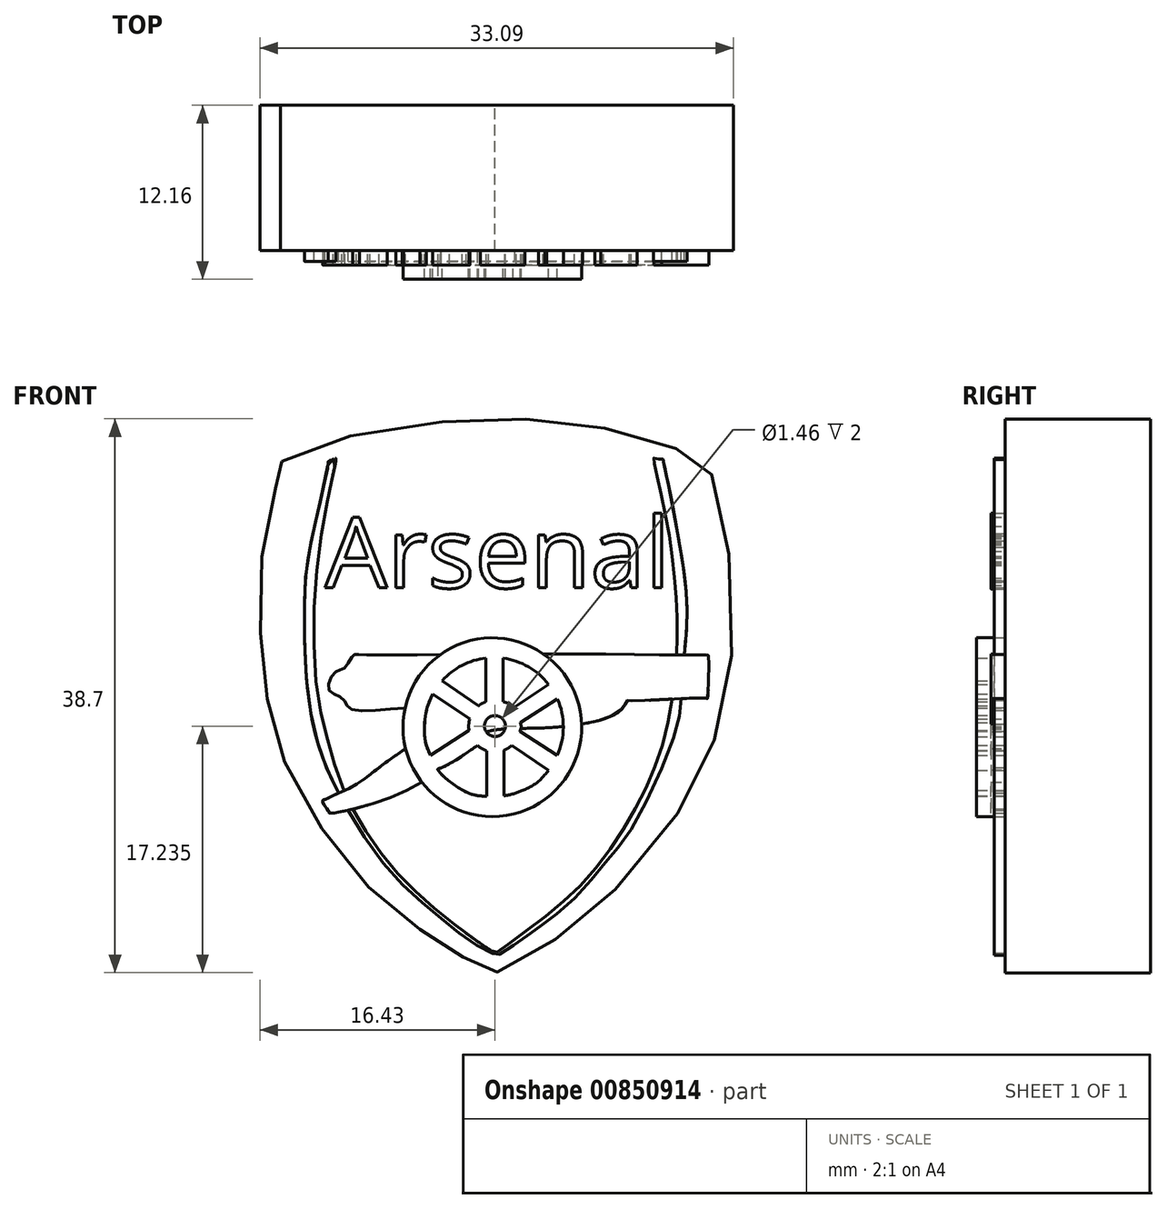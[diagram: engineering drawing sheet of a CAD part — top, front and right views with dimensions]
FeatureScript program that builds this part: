
annotation { "Feature Type Name" : "Feature", "Feature Type Description" : "" }
export const myFeature = defineFeature(function(context is Context, id is Id, definition is map)
    precondition{}
    {
        {
            var Q0;
            Q0=qCreatedBy(makeId("Front.planeOp"),FACE);
            var sketch = newSketch(context, id + "F0", { "sketchPlane" : qUnion([Q0])});
            skPoint(sketch, "E0.12.internal.snap0", {"position": v(20, 0) * mm});
            skPoint(sketch, "E0.13.internal.snap0", {"position": v(20, 0) * mm});
            skFitSpline(sketch, "E0", {"points": [v(5.13, 36.38) * mm, v(10.44, 38.27) * mm, v(18.73, 39.3) * mm, v(25.28, 39.07) * mm, v(31.25, 37.76) * mm, v(34.45, 36.38) * mm, v(35.25, 35.22) * mm, v(36.63, 27) * mm, v(35.76, 18.33) * mm, v(33.07, 12.22) * mm, v(27.1, 5.16) * mm, v(22.66, 2.04) * mm, v(20, 0.64) * mm, v(20, 0.66) * mm, v(18.14, 1.55) * mm, v(16.5, 2.5) * mm, v(13.05, 4.95) * mm, v(9.94, 7.99) * mm, v(6.24, 13.42) * mm, v(4.58, 17.65) * mm, v(3.79, 21.95) * mm, v(3.6, 26.79) * mm, v(4.19, 32.94) * mm, v(4.98, 35.32) * mm, v(5.05, 35.81) * mm, v(5.13, 36.38) * mm]});
            skSolve(sketch);
        }
        {
            var Q0;
            Q0=makeQuery(id+"F0.imprint","IMPRINT",FACE,{"disambiguationData":[TD([[makeQuery(id+"F0.imprint","IMPRINT",EDGE,{"derivedFrom":sQuery(id+"F0.wireOp",EDGE,"E0")}),-1.0]])]});
            extrude(context, id + "F1", {"entities" : qUnion([Q0]), "depth" : 10.16 * mm, "offsetDistance" : 25 * mm});
        }
        {
            var Q0;
            {var subQ0=sQuery(id+"F0.wireOp",EDGE,"E0");Q0=makeQuery(id+"FBtWP9GjsR8Dhei_1.boolean.opBoolean","SPLIT",FACE,{"disambiguationData":[TD([makeQuery(id+"F1.opExtrude","SWEPT_FACE",FACE,{"disambiguationData":[OSD([subQ0])]})])],"derivedFrom":makeQuery(id+"F1.opExtrude","CAP_FACE",FACE,{"disambiguationData":[OSD([subQ0])],"isStart":false})});}
            var sketch = newSketch(context, id + "F2", { "sketchPlane" : qUnion([Q0])});
            skCircle(sketch, "E1", {"center": v(19.82, 17.8) * mm, "radius": 6.24 * mm});
            skPoint(sketch, "E1.first.point", {"position": v(19.26, 24.01) * mm});
            skPoint(sketch, "E1.second.point", {"position": v(20.58, 11.6) * mm});
            skPoint(sketch, "E1.third.point", {"position": v(24.98, 14.28) * mm});
            skArc(sketch, "E2", {"start": v(19.38, 22.63) * mm, "mid": v(17.7, 22.12) * mm, "end": v(16.32, 21.05) * mm});
            skPoint(sketch, "E2.first.point", {"position": v(21.94, 13.38) * mm});
            skPoint(sketch, "E2.second.point", {"position": v(17.75, 22.14) * mm});
            skPoint(sketch, "E2.third.point", {"position": v(23, 21.57) * mm});
            skPoint(sketch, "E3.first.point", {"position": v(20.88, 19.43) * mm});
            skPoint(sketch, "E3.second.point", {"position": v(18.17, 17.84) * mm});
            skPoint(sketch, "E3.third.point", {"position": v(18.99, 16.36) * mm});
            skCircle(sketch, "E4", {"center": v(20, 17.87) * mm, "radius": 0.73 * mm});
            skPoint(sketch, "E4.first.point", {"position": v(20.04, 17.14) * mm});
            skPoint(sketch, "E4.second.point", {"position": v(19.68, 18.53) * mm});
            skPoint(sketch, "E4.third.point", {"position": v(20.7, 18.1) * mm});
            skLineSegment(sketch, "E5", {"start": v(16.32, 21.05) * mm, "end": v(18.86, 19.29) * mm});
            skLineSegment(sketch, "E6", {"start": v(15.67, 20.13) * mm, "end": v(18.24, 18.37) * mm});
            skLineSegment(sketch, "E7", {"start": v(15.48, 15.84) * mm, "end": v(18.2, 17.58) * mm});
            skLineSegment(sketch, "E8", {"start": v(19.44, 12.97) * mm, "end": v(19.44, 16.14) * mm});
            skLineSegment(sketch, "E9", {"start": v(20.63, 16.18) * mm, "end": v(20.63, 13) * mm});
            skLineSegment(sketch, "E10", {"start": v(21.19, 16.53) * mm, "end": v(23.74, 14.78) * mm});
            skLineSegment(sketch, "E11", {"start": v(21.75, 17.52) * mm, "end": v(24.37, 15.82) * mm});
            skLineSegment(sketch, "E12", {"start": v(21.77, 18.1) * mm, "end": v(24.37, 19.78) * mm});
            skLineSegment(sketch, "E13", {"start": v(21.28, 19.13) * mm, "end": v(23.76, 20.8) * mm});
            skLineSegment(sketch, "E14", {"start": v(20.58, 19.57) * mm, "end": v(20.58, 22.62) * mm});
            skLineSegment(sketch, "E15", {"start": v(19.38, 19.57) * mm, "end": v(19.38, 22.63) * mm});
            skArc(sketch, "E16.trimOffspring", {"start": v(24.37, 15.82) * mm, "mid": v(24.79, 17.8) * mm, "end": v(24.37, 19.78) * mm});
            skArc(sketch, "E17.trimOffspring", {"start": v(20.63, 13) * mm, "mid": v(21.3, 13.14) * mm, "end": v(21.94, 13.38) * mm});
            skArc(sketch, "E18.trimOffspring", {"start": v(23.76, 20.8) * mm, "mid": v(22.35, 22.02) * mm, "end": v(20.58, 22.62) * mm});
            skArc(sketch, "E19.trimOffspring", {"start": v(20.63, 16.18) * mm, "mid": v(20.92, 16.33) * mm, "end": v(21.19, 16.53) * mm});
            skArc(sketch, "E20.trimOffspring", {"start": v(18.24, 18.37) * mm, "mid": v(18.18, 17.98) * mm, "end": v(18.2, 17.58) * mm});
            skArc(sketch, "E21.trimOffspring", {"start": v(18.79, 16.51) * mm, "mid": v(19.1, 16.3) * mm, "end": v(19.44, 16.14) * mm});
            skFitSpline(sketch, "E22", {"points": [v(15.67, 20.13) * mm, v(15.23, 18.98) * mm, v(15.12, 16.98) * mm, v(15.48, 15.84) * mm], "startDerivative": vector(-1.6, -3.33) * mm, "endDerivative": vector(1.47, -3.34) * mm});
            skFitSpline(sketch, "E23", {"points": [v(21.94, 13.38) * mm, v(22.95, 13.92) * mm, v(23.74, 14.78) * mm], "startDerivative": vector(2.14, 0.94) * mm, "endDerivative": vector(1.45, 1.87) * mm});
            skFitSpline(sketch, "E24", {"points": [v(21.75, 17.52) * mm, v(21.84, 17.84) * mm, v(21.77, 18.1) * mm], "startDerivative": vector(0.25, 0.63) * mm, "endDerivative": vector(-0.22, 0.55) * mm});
            skFitSpline(sketch, "E25", {"points": [v(18.86, 19.29) * mm, v(19.04, 19.42) * mm, v(19.38, 19.57) * mm], "startDerivative": vector(0.37, 0.32) * mm, "endDerivative": vector(0.66, 0.26) * mm});
            skFitSpline(sketch, "E26", {"points": [v(20.58, 19.57) * mm, v(20.97, 19.43) * mm, v(21.28, 19.13) * mm], "startDerivative": vector(0.83, -0.2) * mm, "endDerivative": vector(0.56, -0.68) * mm});
            skFitSpline(sketch, "E27", {"points": [v(18.79, 16.51) * mm, v(16.25, 14.96) * mm, v(16, 14.84) * mm, v(17.83, 13.35) * mm, v(19.44, 12.97) * mm], "startDerivative": vector(-9, -6.14) * mm, "endDerivative": vector(5.67, -0.22) * mm});
            skSolve(sketch);
        }
        {
            var Q0;
            Q0=makeQuery(id+"F1.opExtrude","CAP_FACE",FACE,{"disambiguationData":[OSD([sQuery(id+"F0.wireOp",EDGE,"E0")])],"isStart":false});
            var sketch = newSketch(context, id + "F3", { "sketchPlane" : qUnion([Q0])});
            skText(sketch, "E28", { "text": "Arsenal\n", "fontName": "OpenSans-Regular.ttf"});
            skFitSpline(sketch, "E29", {"points": [v(7.96, 12.63) * mm, v(8.4, 11.87) * mm, v(8.45, 11.79) * mm, v(14.58, 13.76) * mm, v(18.73, 17.2) * mm, v(23.3, 17.74) * mm, v(28.72, 18.91) * mm, v(29.25, 19.65) * mm, v(29.44, 19.65) * mm, v(34.8, 19.81) * mm, v(34.87, 19.81) * mm, v(34.92, 22.82) * mm, v(34.8, 22.87) * mm, v(23.65, 22.92) * mm, v(10.5, 22.87) * mm, v(10.1, 22.8) * mm, v(9.45, 21.91) * mm, v(8.85, 21.66) * mm, v(8.4, 20.42) * mm, v(9.4, 19.78) * mm, v(10.03, 19.02) * mm, v(14.77, 18.95) * mm, v(14.83, 17.36) * mm, v(12.86, 15.67) * mm, v(10.12, 13.7) * mm, v(8.6, 12.97) * mm, v(8.16, 12.75) * mm, v(7.96, 12.63) * mm]});
            const initialGuessF3  = {"E28": [0.00813, 0.02753, 1, 0, 0.00496]};
            skSetInitialGuess(sketch, initialGuessF3);
            skSolve(sketch);
        }
        {
            var Q0;
            Q0=makeQuery(id+"F2.imprint","IMPRINT",FACE,{"disambiguationData":[TD([[makeQuery(id+"F2.imprint","IMPRINT",EDGE,{"derivedFrom":sQuery(id+"F2.wireOp",EDGE,"E1")}),1.0]])]});
            extrude(context, id + "F4", {"entities" : qUnion([Q0]), "operationType" : NewBodyOperationType.ADD, "depth" : 2 * mm, "offsetDistance" : 25 * mm});
        }
        {
            var Q0;
            Q0=qSketchRegion(id+"F3",true);
            extrude(context, id + "F5", {"entities" : qUnion([Q0]), "operationType" : NewBodyOperationType.ADD, "depth" : 1 * mm, "offsetDistance" : 25 * mm});
        }
        {
            var Q0;
            Q0=makeQuery(id+"F3.imprint","IMPRINT",FACE,{"disambiguationData":[TD([[makeQuery(id+"F3.imprint","IMPRINT",EDGE,{"derivedFrom":sQuery(id+"F3.wireOp",EDGE,"E28.sketch_text.stroke-0")}),1.0]])]});
            var sketch = newSketch(context, id + "F6", { "sketchPlane" : qUnion([Q0])});
            skFitSpline(sketch, "E30", {"points": [v(8.35, 36.26) * mm, v(7.07, 30.22) * mm, v(6.7, 26.05) * mm, v(6.93, 20.24) * mm, v(7.8, 16.17) * mm, v(9.08, 13.2) * mm, v(12.46, 7.96) * mm, v(15.94, 4.7) * mm, v(18.6, 2.65) * mm, v(20.08, 1.88) * mm, v(20.2, 1.87) * mm, v(21.64, 2.77) * mm, v(22.96, 3.73) * mm, v(25.4, 5.67) * mm, v(27.8, 8.42) * mm, v(29.58, 10.77) * mm, v(32.61, 17.42) * mm, v(33.01, 19.85) * mm, v(33.3, 23.5) * mm, v(33.26, 28.26) * mm, v(31.74, 36.54) * mm, v(31.73, 36.52) * mm, v(31.15, 36.6) * mm, v(31.1, 36.58) * mm, v(31.8, 33.24) * mm, v(32.71, 26.08) * mm, v(32.48, 20.45) * mm, v(31.43, 15.7) * mm, v(29.4, 11.37) * mm, v(26.45, 7.23) * mm, v(22.8, 4.03) * mm, v(20.16, 2.08) * mm, v(20, 2.05) * mm, v(16.84, 4.27) * mm, v(12.7, 8.2) * mm, v(9.54, 13.15) * mm, v(8.52, 16.22) * mm, v(7.7, 19.44) * mm, v(7.35, 24.9) * mm, v(7.81, 30.85) * mm, v(8.52, 34.58) * mm, v(8.69, 35.43) * mm, v(8.9, 36.58) * mm, v(8.86, 36.58) * mm, v(8.37, 36.41) * mm, v(8.35, 36.26) * mm]});
            skSolve(sketch);
        }
        {
            var Q0;
            Q0=qSketchRegion(id+"F6",true);
            extrude(context, id + "F7", {"entities" : qUnion([Q0]), "operationType" : NewBodyOperationType.ADD, "depth" : 0.76 * mm, "offsetDistance" : 25 * mm});
        }
    });
